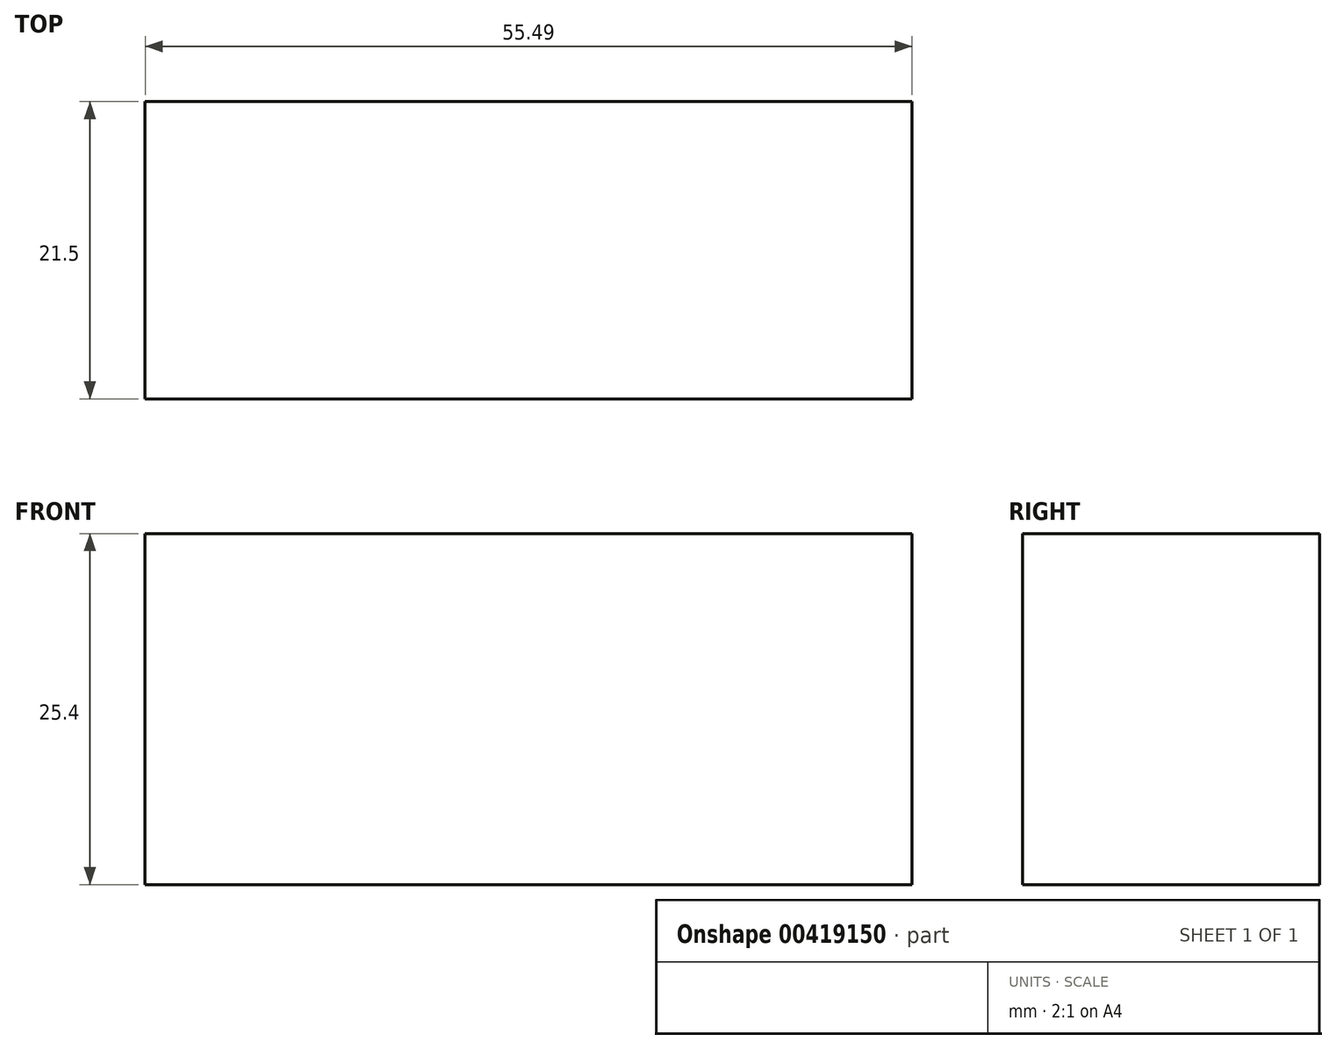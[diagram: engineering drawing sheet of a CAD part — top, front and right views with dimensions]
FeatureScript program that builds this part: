
annotation { "Feature Type Name" : "Feature", "Feature Type Description" : "" }
export const myFeature = defineFeature(function(context is Context, id is Id, definition is map)
    precondition{}
    {
        {
            var Q0;
            Q0=qCreatedBy(makeId("Top.planeOp"),FACE);
            var sketch = newSketch(context, id + "F0", { "sketchPlane" : qUnion([Q0])});
            skLineSegment(sketch, "E0.bottom", {"start": v(-75.24, 31.09) * mm, "end": v(-19.75, 31.09) * mm});
            skLineSegment(sketch, "E0.top", {"start": v(-75.24, 52.59) * mm, "end": v(-19.75, 52.59) * mm});
            skLineSegment(sketch, "E0.left", {"start": v(-75.24, 31.09) * mm, "end": v(-75.24, 52.59) * mm});
            skLineSegment(sketch, "E0.right", {"start": v(-19.75, 31.09) * mm, "end": v(-19.75, 52.59) * mm});
            skSolve(sketch);
        }
        {
            var Q0;
            Q0=makeQuery(id+"F0.imprint","IMPRINT",FACE,{"disambiguationData":[TD([[makeQuery(id+"F0.imprint","IMPRINT",EDGE,{"derivedFrom":sQuery(id+"F0.wireOp",EDGE,"E0.bottom")}),1.0]])]});
            extrude(context, id + "F1", {"entities" : qUnion([Q0]), "depth" : 25.4 * mm});
        }
    });
